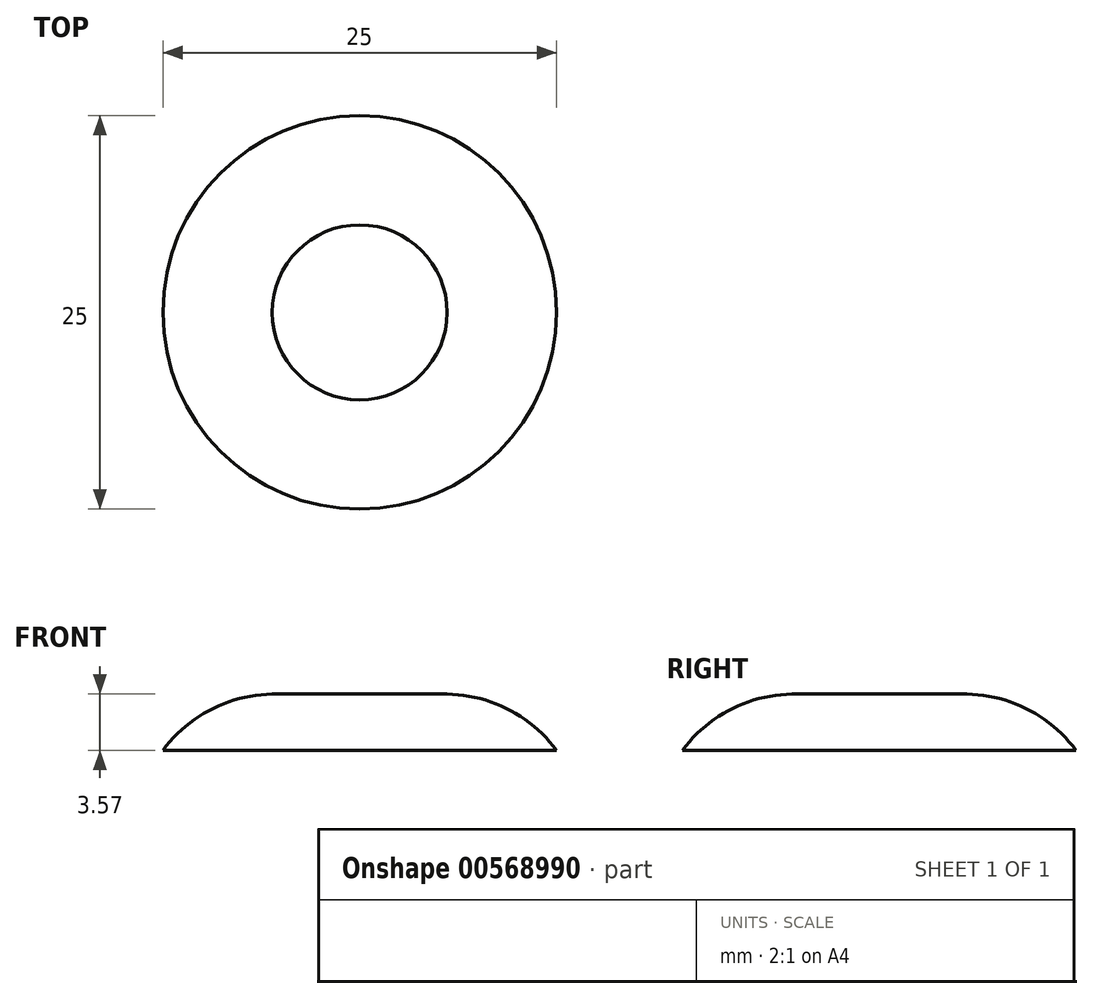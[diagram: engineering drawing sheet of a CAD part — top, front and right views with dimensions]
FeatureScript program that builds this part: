
annotation { "Feature Type Name" : "Feature", "Feature Type Description" : "" }
export const myFeature = defineFeature(function(context is Context, id is Id, definition is map)
    precondition{}
    {
        {
            var Q0;
            Q0=qCreatedBy(makeId("Front.planeOp"),FACE);
            var sketch = newSketch(context, id + "F0", { "sketchPlane" : qUnion([Q0])});
            skLineSegment(sketch, "E0", {"start": v(-12.5, -32.24) * mm, "end": v(12.5, -32.24) * mm});
            skLineSegment(sketch, "E1", {"start": v(-5.56, -28.67) * mm, "end": v(5.56, -28.67) * mm});
            skArc(sketch, "E2", {"start": v(-5.56, -28.67) * mm, "mid": v(-9.44, -29.64) * mm, "end": v(-12.5, -32.24) * mm});
            skArc(sketch, "E3", {"start": v(12.5, -32.24) * mm, "mid": v(9.44, -29.64) * mm, "end": v(5.56, -28.67) * mm});
            skLineSegment(sketch, "E4", {"start": v(0, -28.67) * mm, "end": v(0, -32.24) * mm});
            skSolve(sketch);
        }
        {
            var Q0;
            {var subQ0=sQuery(id+"F0.wireOp",EDGE,"E3");Q0=makeQuery(id+"F0.imprint","IMPRINT",FACE,{"disambiguationData":[TD([[makeQuery(id+"F0.imprint","IMPRINT",EDGE,{"derivedFrom":subQ0}),1.0]])]});}
            var Q1;
            Q1=sQuery(id+"F0.wireOp",EDGE,"E4");
            revolve(context, id + "F1", {"entities" : qUnion([Q0]), "axis" : qUnion([Q1]), "revolveType" : RevolveType.FULL});
        }
    });
